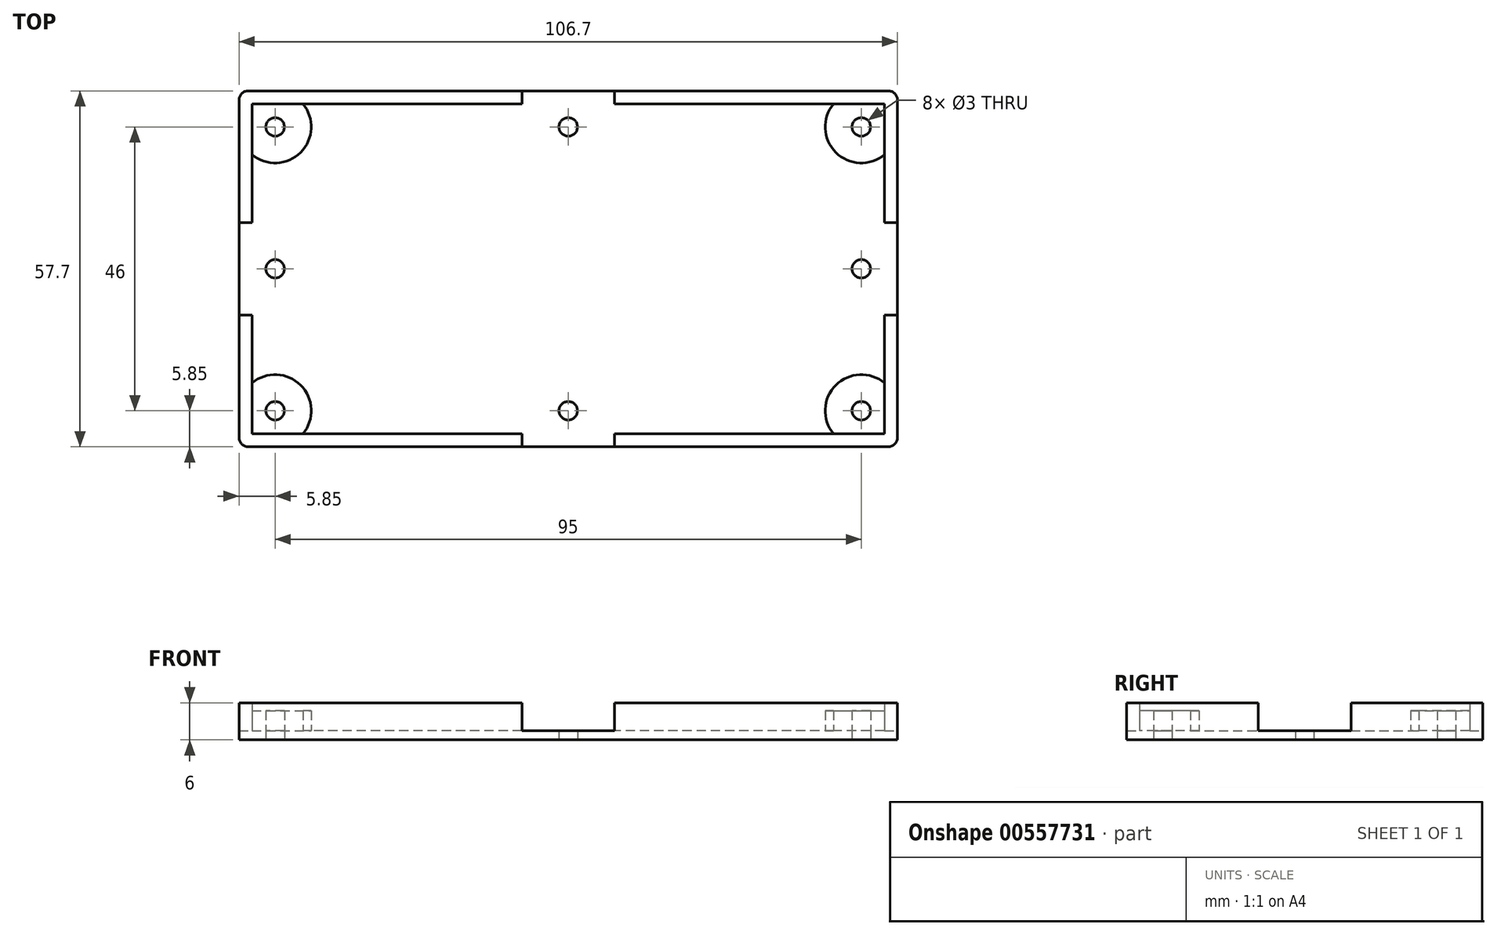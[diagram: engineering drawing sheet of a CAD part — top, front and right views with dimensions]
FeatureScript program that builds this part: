
annotation { "Feature Type Name" : "Feature", "Feature Type Description" : "" }
export const myFeature = defineFeature(function(context is Context, id is Id, definition is map)
    precondition{}
    {
        {
            assignVariable(context, id + "F0", {"name" : "Grosor", "anyValue" : 1.3});
        }
        {
            assignVariable(context, id + "F1", {"name" : "Paredes", "anyValue" : 2.1});
        }
        {
            var Q0;
            Q0=qCreatedBy(makeId("Top.planeOp"),FACE);
            var sketch = newSketch(context, id + "F2", { "sketchPlane" : qUnion([Q0])});
            skLineSegment(sketch, "E0.bottom", {"start": v(-51.25, 26.75) * mm, "end": v(51.25, 26.75) * mm});
            skLineSegment(sketch, "E0.top", {"start": v(-43.01, -26.75) * mm, "end": v(51.25, -26.75) * mm});
            skLineSegment(sketch, "E0.left", {"start": v(-51.25, 26.75) * mm, "end": v(-51.25, -18.51) * mm});
            skLineSegment(sketch, "E0.right", {"start": v(51.25, 26.75) * mm, "end": v(51.25, -26.75) * mm});
            skPoint(sketch, "E0.middle", {"position": v(0, 0) * mm});
            skLineSegment(sketch, "E1.0", {"start": v(-53.35, -28.85) * mm, "end": v(53.35, -28.85) * mm});
            skLineSegment(sketch, "E1.1", {"start": v(-53.35, 28.85) * mm, "end": v(-53.35, -28.85) * mm});
            skLineSegment(sketch, "E1.2", {"start": v(-53.35, 28.85) * mm, "end": v(53.35, 28.85) * mm});
            skLineSegment(sketch, "E1.3", {"start": v(53.35, 28.85) * mm, "end": v(53.35, -28.85) * mm});
            skLineSegment(sketch, "E2.bottom", {"start": v(-47.5, 23) * mm, "end": v(47.5, 23) * mm, "construction": true});
            skLineSegment(sketch, "E2.top", {"start": v(-47.5, -23) * mm, "end": v(47.5, -23) * mm, "construction": true});
            skLineSegment(sketch, "E2.left", {"start": v(-47.5, 23) * mm, "end": v(-47.5, -23) * mm, "construction": true});
            skLineSegment(sketch, "E2.right", {"start": v(47.5, 23) * mm, "end": v(47.5, -23) * mm, "construction": true});
            skCircle(sketch, "E3", {"center": v(47.5, 23) * mm, "radius": 1.5 * mm});
            skCircle(sketch, "E4", {"center": v(47.5, -23) * mm, "radius": 1.5 * mm});
            skCircle(sketch, "E5", {"center": v(-47.5, -23) * mm, "radius": 1.5 * mm});
            skCircle(sketch, "E6", {"center": v(-47.5, 23) * mm, "radius": 1.5 * mm});
            skArc(sketch, "E7", {"start": v(-51.25, 18.51) * mm, "mid": v(-43.36, 18.86) * mm, "end": v(-43.01, 26.75) * mm});
            skArc(sketch, "E8", {"start": v(43.01, 26.75) * mm, "mid": v(43.36, 18.86) * mm, "end": v(51.25, 18.51) * mm});
            skArc(sketch, "E9", {"start": v(51.25, -18.51) * mm, "mid": v(43.36, -18.86) * mm, "end": v(43.01, -26.75) * mm});
            skArc(sketch, "E10.trimOffspring", {"start": v(-43.01, -26.75) * mm, "mid": v(-43.36, -18.86) * mm, "end": v(-51.25, -18.51) * mm});
            skPoint(sketch, "E11.orphan", {"position": v(-51.25, -26.75) * mm});
            skLineSegment(sketch, "E12", {"start": v(-51.25, -18.51) * mm, "end": v(-51.25, -26.75) * mm});
            skLineSegment(sketch, "E13", {"start": v(-43.01, -26.75) * mm, "end": v(-51.25, -26.75) * mm});
            skLineSegment(sketch, "E14.bottom", {"start": v(53.35, -7.5) * mm, "end": v(-53.35, -7.5) * mm});
            skLineSegment(sketch, "E14.top", {"start": v(53.35, 7.5) * mm, "end": v(-53.35, 7.5) * mm});
            skLineSegment(sketch, "E14.left", {"start": v(53.35, -7.5) * mm, "end": v(53.35, 7.5) * mm});
            skLineSegment(sketch, "E14.right", {"start": v(-53.35, -7.5) * mm, "end": v(-53.35, 7.5) * mm});
            skLineSegment(sketch, "E15.bottom", {"start": v(-7.5, 28.85) * mm, "end": v(7.5, 28.85) * mm});
            skLineSegment(sketch, "E15.top", {"start": v(-7.5, -28.85) * mm, "end": v(7.5, -28.85) * mm});
            skLineSegment(sketch, "E15.left", {"start": v(-7.5, 28.85) * mm, "end": v(-7.5, -28.85) * mm});
            skLineSegment(sketch, "E15.right", {"start": v(7.5, 28.85) * mm, "end": v(7.5, -28.85) * mm});
            skCircle(sketch, "E16", {"center": v(-47.5, 0) * mm, "radius": 1.5 * mm});
            skCircle(sketch, "E17", {"center": v(0, 23) * mm, "radius": 1.5 * mm});
            skCircle(sketch, "E18", {"center": v(0, -23) * mm, "radius": 1.5 * mm});
            skCircle(sketch, "E19", {"center": v(47.5, 0) * mm, "radius": 1.5 * mm});
            skSolve(sketch);
        }
        {
            var Q0;
            {var subQ0=sQuery(id+"F2.wireOp",EDGE,"E0.right");var subQ1=sQuery(id+"F2.wireOp",EDGE,"E0.top");var subQ3=sQuery(id+"F2.wireOp",EDGE,"E9");var subQ5=makeQuery(id+"F2.imprint","INTERSECT",VERTEX,{"derivedFrom":[subQ1,subQ3]});var subQ6=sQuery(id+"F2.wireOp",EDGE,"E15.right");var subQ17=sQuery(id+"F2.wireOp",EDGE,"E0.bottom");var subQ18=makeQuery(id+"F2.imprint","INTERSECT",VERTEX,{"derivedFrom":[subQ17,subQ6]});var subQ19=sQuery(id+"F2.wireOp",EDGE,"E15.left");var subQ26=makeQuery(id+"F2.imprint","INTERSECT",VERTEX,{"derivedFrom":[subQ1,subQ19]});var subQ32=sQuery(id+"F2.wireOp",EDGE,"E12");var subQ34=sQuery(id+"F2.wireOp",EDGE,"E0.left");var subQ42=sQuery(id+"F2.wireOp",EDGE,"E14.top");var subQ44=makeQuery(id+"F2.imprint","INTERSECT",VERTEX,{"derivedFrom":[subQ0,subQ42]});var subQ47=makeQuery(id+"F2.imprint","INTERSECT",VERTEX,{"derivedFrom":[subQ34,subQ42]});var subQ50=sQuery(id+"F2.wireOp",EDGE,"E7");var subQ53=makeQuery(id+"F2.imprint","INTERSECT",VERTEX,{"derivedFrom":[subQ17,subQ50]});Q0=qUnion([makeQuery(id+"F2.imprint","IMPRINT",FACE,{"disambiguationData":[TD([[makeQuery(id+"F2.imprint","IMPRINT",EDGE,{"disambiguationData":[TD([[subQ53,-1.0]])],"derivedFrom":subQ17}),1.0]])]}),makeQuery(id+"F2.imprint","IMPRINT",FACE,{"disambiguationData":[TD([[makeQuery(id+"F2.imprint","IMPRINT",EDGE,{"disambiguationData":[TD([[subQ47,-1.0]])],"derivedFrom":subQ34}),-1.0]])]}),makeQuery(id+"F2.imprint","IMPRINT",FACE,{"disambiguationData":[TD([[makeQuery(id+"F2.imprint","IMPRINT",EDGE,{"disambiguationData":[TD([[subQ44,-1.0]])],"derivedFrom":subQ0}),1.0]])]}),makeQuery(id+"F2.imprint","IMPRINT",FACE,{"disambiguationData":[TD([[makeQuery(id+"F2.imprint","IMPRINT",EDGE,{"disambiguationData":[TD([[subQ18,-1.0]])],"derivedFrom":subQ17}),1.0]])]}),makeQuery(id+"F2.imprint","IMPRINT",FACE,{"disambiguationData":[TD([[makeQuery(id+"F2.imprint","IMPRINT",EDGE,{"derivedFrom":subQ32}),-1.0]])]}),makeQuery(id+"F2.imprint","IMPRINT",FACE,{"disambiguationData":[TD([[makeQuery(id+"F2.imprint","IMPRINT",EDGE,{"disambiguationData":[TD([[subQ26,-1.0]])],"derivedFrom":subQ1}),-1.0]])]}),makeQuery(id+"F2.imprint","IMPRINT",FACE,{"disambiguationData":[TD([[makeQuery(id+"F2.imprint","IMPRINT",EDGE,{"disambiguationData":[TD([[subQ18,1.0]])],"derivedFrom":subQ17}),1.0]])]}),makeQuery(id+"F2.imprint","IMPRINT",FACE,{"disambiguationData":[TD([[makeQuery(id+"F2.imprint","IMPRINT",EDGE,{"disambiguationData":[TD([[subQ5,1.0]])],"derivedFrom":subQ1}),-1.0]])]})]);}
            var Q1;
            {var subQ0=sQuery(id+"F2.wireOp",EDGE,"E10.trimOffspring");Q1=makeQuery(id+"F2.imprint","IMPRINT",FACE,{"disambiguationData":[TD([[makeQuery(id+"F2.imprint","IMPRINT",EDGE,{"derivedFrom":subQ0}),-1.0]])]});}
            var Q2;
            Q2=makeQuery(id+"F2.imprint","IMPRINT",FACE,{"disambiguationData":[TD([[makeQuery(id+"F2.imprint","IMPRINT",EDGE,{"derivedFrom":sQuery(id+"F2.wireOp",EDGE,"E6")}),-1.0]])]});
            var Q3;
            Q3=makeQuery(id+"F2.imprint","IMPRINT",FACE,{"disambiguationData":[TD([[makeQuery(id+"F2.imprint","IMPRINT",EDGE,{"derivedFrom":sQuery(id+"F2.wireOp",EDGE,"E3")}),-1.0]])]});
            var Q4;
            Q4=makeQuery(id+"F2.imprint","IMPRINT",FACE,{"disambiguationData":[TD([[makeQuery(id+"F2.imprint","IMPRINT",EDGE,{"derivedFrom":sQuery(id+"F2.wireOp",EDGE,"E4")}),-1.0]])]});
            var Q5;
            Q5=makeQuery(id+"F2.imprint","IMPRINT",FACE,{"disambiguationData":[TD([[makeQuery(id+"F2.imprint","IMPRINT",EDGE,{"derivedFrom":sQuery(id+"F2.wireOp",EDGE,"E5")}),-1.0]])]});
            var Q6;
            Q6=makeQuery(id+"F2.imprint","IMPRINT",FACE,{"disambiguationData":[TD([[makeQuery(id+"F2.imprint","IMPRINT",EDGE,{"derivedFrom":sQuery(id+"F2.wireOp",EDGE,"E16")}),-1.0]])]});
            var Q7;
            {var subQ0=sQuery(id+"F2.wireOp",EDGE,"E7");Q7=makeQuery(id+"F2.imprint","IMPRINT",FACE,{"disambiguationData":[TD([[makeQuery(id+"F2.imprint","IMPRINT",EDGE,{"derivedFrom":subQ0}),-1.0]])]});}
            var Q8;
            Q8=makeQuery(id+"F2.imprint","IMPRINT",FACE,{"disambiguationData":[TD([[makeQuery(id+"F2.imprint","IMPRINT",EDGE,{"derivedFrom":sQuery(id+"F2.wireOp",EDGE,"E17")}),-1.0]])]});
            var Q9;
            {var subQ7=sQuery(id+"F2.wireOp",EDGE,"E8");Q9=makeQuery(id+"F2.imprint","IMPRINT",FACE,{"disambiguationData":[TD([[makeQuery(id+"F2.imprint","IMPRINT",EDGE,{"derivedFrom":subQ7}),-1.0]])]});}
            var Q10;
            Q10=makeQuery(id+"F2.imprint","IMPRINT",FACE,{"disambiguationData":[TD([[makeQuery(id+"F2.imprint","IMPRINT",EDGE,{"derivedFrom":sQuery(id+"F2.wireOp",EDGE,"E19")}),-1.0]])]});
            var Q11;
            {var subQ0=sQuery(id+"F2.wireOp",EDGE,"E9");Q11=makeQuery(id+"F2.imprint","IMPRINT",FACE,{"disambiguationData":[TD([[makeQuery(id+"F2.imprint","IMPRINT",EDGE,{"derivedFrom":subQ0}),-1.0]])]});}
            var Q12;
            Q12=makeQuery(id+"F2.imprint","IMPRINT",FACE,{"disambiguationData":[TD([[makeQuery(id+"F2.imprint","IMPRINT",EDGE,{"derivedFrom":sQuery(id+"F2.wireOp",EDGE,"E18")}),-1.0]])]});
            var Q13;
            {var subQ0=sQuery(id+"F2.wireOp",EDGE,"E15.left");var subQ1=sQuery(id+"F2.wireOp",EDGE,"E14.bottom");var subQ2=makeQuery(id+"F2.imprint","INTERSECT",VERTEX,{"derivedFrom":[subQ1,subQ0]});Q13=makeQuery(id+"F2.imprint","IMPRINT",FACE,{"disambiguationData":[TD([[makeQuery(id+"F2.imprint","IMPRINT",EDGE,{"disambiguationData":[TD([[subQ2,1.0]])],"derivedFrom":subQ1}),-1.0]])]});}
            extrude(context, id + "F3", {"entities" : qUnion([Q0, Q1, Q2, Q3, Q4, Q5, Q6, Q7, Q8, Q9, Q10, Q11, Q12, Q13]), "depth" : (getVariable(context, 'Paredes') - 0.6) * mm, "offsetDistance" : 25 * mm});
        }
        {
            var Q0;
            Q0=makeQuery(id+"F2.imprint","IMPRINT",FACE,{"disambiguationData":[TD([[makeQuery(id+"F2.imprint","IMPRINT",EDGE,{"derivedFrom":sQuery(id+"F2.wireOp",EDGE,"E5")}),-1.0]])]});
            var Q1;
            Q1=makeQuery(id+"F2.imprint","IMPRINT",FACE,{"disambiguationData":[TD([[makeQuery(id+"F2.imprint","IMPRINT",EDGE,{"derivedFrom":sQuery(id+"F2.wireOp",EDGE,"E4")}),-1.0]])]});
            var Q2;
            Q2=makeQuery(id+"F2.imprint","IMPRINT",FACE,{"disambiguationData":[TD([[makeQuery(id+"F2.imprint","IMPRINT",EDGE,{"derivedFrom":sQuery(id+"F2.wireOp",EDGE,"E3")}),-1.0]])]});
            var Q3;
            Q3=makeQuery(id+"F2.imprint","IMPRINT",FACE,{"disambiguationData":[TD([[makeQuery(id+"F2.imprint","IMPRINT",EDGE,{"derivedFrom":sQuery(id+"F2.wireOp",EDGE,"E6")}),-1.0]])]});
            extrude(context, id + "F4", {"entities" : qUnion([Q0, Q1, Q2, Q3]), "operationType" : NewBodyOperationType.ADD, "depth" : (getVariable(context, 'Paredes') + (getVariable(context, 'Grosor') * 2)) * mm, "offsetDistance" : 25 * mm});
        }
        {
            var Q0;
            {var subQ5=sQuery(id+"F2.wireOp",EDGE,"E12");Q0=makeQuery(id+"F2.imprint","IMPRINT",FACE,{"disambiguationData":[TD([[makeQuery(id+"F2.imprint","IMPRINT",EDGE,{"derivedFrom":subQ5}),-1.0]])]});}
            var Q1;
            {var subQ1=sQuery(id+"F2.wireOp",EDGE,"E0.top");var subQ3=sQuery(id+"F2.wireOp",EDGE,"E9");var subQ5=makeQuery(id+"F2.imprint","INTERSECT",VERTEX,{"derivedFrom":[subQ1,subQ3]});Q1=makeQuery(id+"F2.imprint","IMPRINT",FACE,{"disambiguationData":[TD([[makeQuery(id+"F2.imprint","IMPRINT",EDGE,{"disambiguationData":[TD([[subQ5,1.0]])],"derivedFrom":subQ1}),-1.0]])]});}
            var Q2;
            {var subQ0=sQuery(id+"F2.wireOp",EDGE,"E7");var subQ3=sQuery(id+"F2.wireOp",EDGE,"E0.bottom");var subQ5=makeQuery(id+"F2.imprint","INTERSECT",VERTEX,{"derivedFrom":[subQ3,subQ0]});Q2=makeQuery(id+"F2.imprint","IMPRINT",FACE,{"disambiguationData":[TD([[makeQuery(id+"F2.imprint","IMPRINT",EDGE,{"disambiguationData":[TD([[subQ5,-1.0]])],"derivedFrom":subQ3}),1.0]])]});}
            var Q3;
            {var subQ3=sQuery(id+"F2.wireOp",EDGE,"E0.bottom");var subQ12=sQuery(id+"F2.wireOp",EDGE,"E15.right");var subQ13=makeQuery(id+"F2.imprint","INTERSECT",VERTEX,{"derivedFrom":[subQ3,subQ12]});Q3=makeQuery(id+"F2.imprint","IMPRINT",FACE,{"disambiguationData":[TD([[makeQuery(id+"F2.imprint","IMPRINT",EDGE,{"disambiguationData":[TD([[subQ13,-1.0]])],"derivedFrom":subQ3}),1.0]])]});}
            extrude(context, id + "F5", {"entities" : qUnion([Q0, Q1, Q2, Q3]), "operationType" : NewBodyOperationType.ADD, "depth" : (getVariable(context, 'Paredes') + (getVariable(context, 'Grosor') * 3)) * mm, "offsetDistance" : 25 * mm});
        }
        {
            var Q0;
            {var subQ0=sQuery(id+"F2.wireOp",EDGE,"E1.3");var subQ1=sQuery(id+"F2.wireOp",EDGE,"E1.0");Q0=makeQuery(id+"F5.boolean.opBoolean","MERGE",EDGE,{"derivedFrom":[makeQuery(id+"F3.opExtrude","SWEPT_EDGE",EDGE,{"disambiguationData":[OSD([subQ1,subQ0])]}),makeQuery(id+"F5.opExtrude","SWEPT_EDGE",EDGE,{"disambiguationData":[OSD([subQ1,subQ0])]})]});}
            var Q1;
            {var subQ0=sQuery(id+"F2.wireOp",EDGE,"E1.3");var subQ1=sQuery(id+"F2.wireOp",EDGE,"E1.2");Q1=makeQuery(id+"F5.boolean.opBoolean","MERGE",EDGE,{"derivedFrom":[makeQuery(id+"F3.opExtrude","SWEPT_EDGE",EDGE,{"disambiguationData":[OSD([subQ1,subQ0])]}),makeQuery(id+"F5.opExtrude","SWEPT_EDGE",EDGE,{"disambiguationData":[OSD([subQ1,subQ0])]})]});}
            var Q2;
            {var subQ0=sQuery(id+"F2.wireOp",EDGE,"E1.2");var subQ1=sQuery(id+"F2.wireOp",EDGE,"E1.1");Q2=makeQuery(id+"F5.boolean.opBoolean","MERGE",EDGE,{"derivedFrom":[makeQuery(id+"F3.opExtrude","SWEPT_EDGE",EDGE,{"disambiguationData":[OSD([subQ1,subQ0])]}),makeQuery(id+"F5.opExtrude","SWEPT_EDGE",EDGE,{"disambiguationData":[OSD([subQ1,subQ0])]})]});}
            var Q3;
            {var subQ0=sQuery(id+"F2.wireOp",EDGE,"E1.1");var subQ1=sQuery(id+"F2.wireOp",EDGE,"E1.0");Q3=makeQuery(id+"F5.boolean.opBoolean","MERGE",EDGE,{"derivedFrom":[makeQuery(id+"F3.opExtrude","SWEPT_EDGE",EDGE,{"disambiguationData":[OSD([subQ1,subQ0])]}),makeQuery(id+"F5.opExtrude","SWEPT_EDGE",EDGE,{"disambiguationData":[OSD([subQ1,subQ0])]})]});}
            fillet(context, id + "F6", {"entities" : qUnion([Q0, Q1, Q2, Q3]), "radius" : 1.5 * mm, "tangentPropagation" : true, "allowEdgeOverflow" : false});
        }
    });
